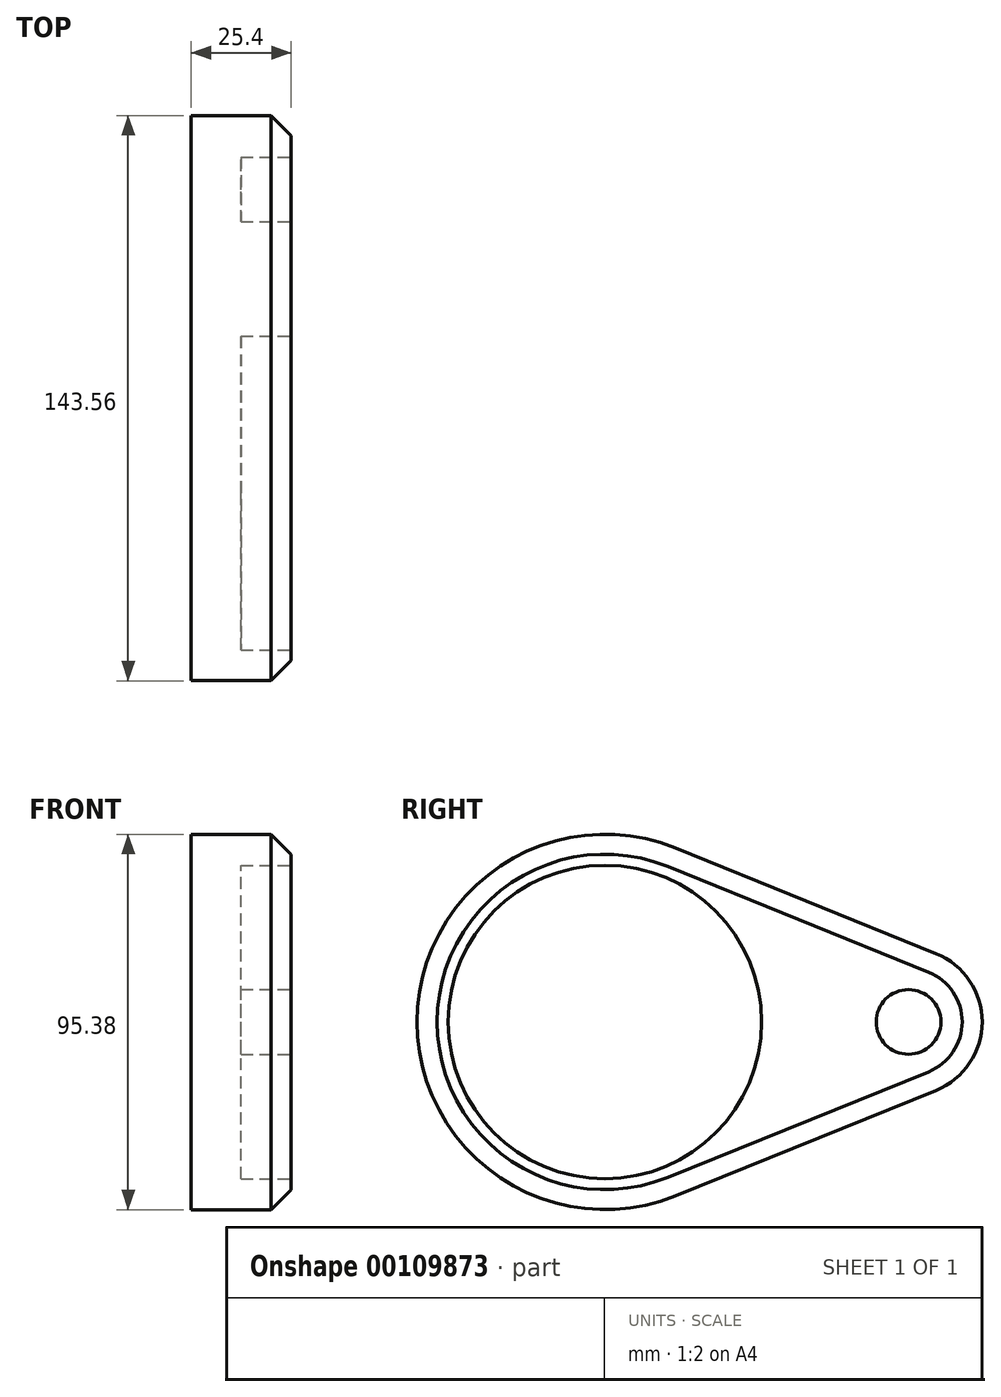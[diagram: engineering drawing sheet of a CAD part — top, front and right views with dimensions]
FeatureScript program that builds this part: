
annotation { "Feature Type Name" : "Feature", "Feature Type Description" : "" }
export const myFeature = defineFeature(function(context is Context, id is Id, definition is map)
    precondition{}
    {
        {
            var Q0;
            Q0=qCreatedBy(makeId("Right.planeOp"),FACE);
            var sketch = newSketch(context, id + "F0", { "sketchPlane" : qUnion([Q0])});
            skCircle(sketch, "E0", {"center": v(0, 0) * mm, "radius": 47.69 * mm});
            skCircle(sketch, "E1", {"center": v(77.15, 0) * mm, "radius": 18.72 * mm});
            skLineSegment(sketch, "E2", {"start": v(84.18, 17.35) * mm, "end": v(17.9, 44.2) * mm});
            skLineSegment(sketch, "E3", {"start": v(84.18, -17.35) * mm, "end": v(17.9, -44.2) * mm});
            skSolve(sketch);
        }
        {
            var Q0;
            Q0 = qSketchRegion(id + "F0", true);
            extrude(context, id + "F1", {"entities" : qUnion([Q0]), "depth" : 25.4 * mm});
        }
        {
            var Q0;
            Q0=makeQuery(id+"F1.opExtrude","CAP_FACE",FACE,{"disambiguationData":[OSD([sQuery(id+"F0.wireOp",EDGE,"E0"),sQuery(id+"F0.wireOp",EDGE,"E1"),sQuery(id+"F0.wireOp",EDGE,"E2"),sQuery(id+"F0.wireOp",EDGE,"E3")])],"isStart":false});
            var sketch = newSketch(context, id + "F2", { "sketchPlane" : qUnion([Q0])});
            skCircle(sketch, "E4", {"center": v(0, 0) * mm, "radius": 39.82 * mm});
            skSolve(sketch);
        }
        {
            var Q0;
            Q0 = qSketchRegion(id + "F2", true);
            extrude(context, id + "F3", {"entities" : qUnion([Q0]), "operationType" : NewBodyOperationType.REMOVE, "oppositeDirection" : true, "depth" : 12.7 * mm});
        }
        {
            var Q0;
            Q0=makeQuery(id+"F1.opExtrude","CAP_FACE",FACE,{"disambiguationData":[OSD([sQuery(id+"F0.wireOp",EDGE,"E0"),sQuery(id+"F0.wireOp",EDGE,"E1"),sQuery(id+"F0.wireOp",EDGE,"E2"),sQuery(id+"F0.wireOp",EDGE,"E3")])],"isStart":false});
            var sketch = newSketch(context, id + "F4", { "sketchPlane" : qUnion([Q0])});
            skCircle(sketch, "E5", {"center": v(77.15, 0) * mm, "radius": 8.21 * mm});
            skSolve(sketch);
        }
        {
            var Q0;
            Q0 = qSketchRegion(id + "F4", true);
            extrude(context, id + "F5", {"entities" : qUnion([Q0]), "operationType" : NewBodyOperationType.REMOVE, "oppositeDirection" : true, "depth" : 12.7 * mm});
        }
        {
            var Q0;
            Q0=makeQuery(id+"F1.opExtrude","CAP_EDGE",EDGE,{"disambiguationData":[OSD([sQuery(id+"F0.wireOp",EDGE,"E2")])],"isStart":false});
            chamfer(context, id + "F6", {"entities" : qUnion([Q0]), "width" : 5.08 * mm, "tangentPropagation" : true});
        }
    });
